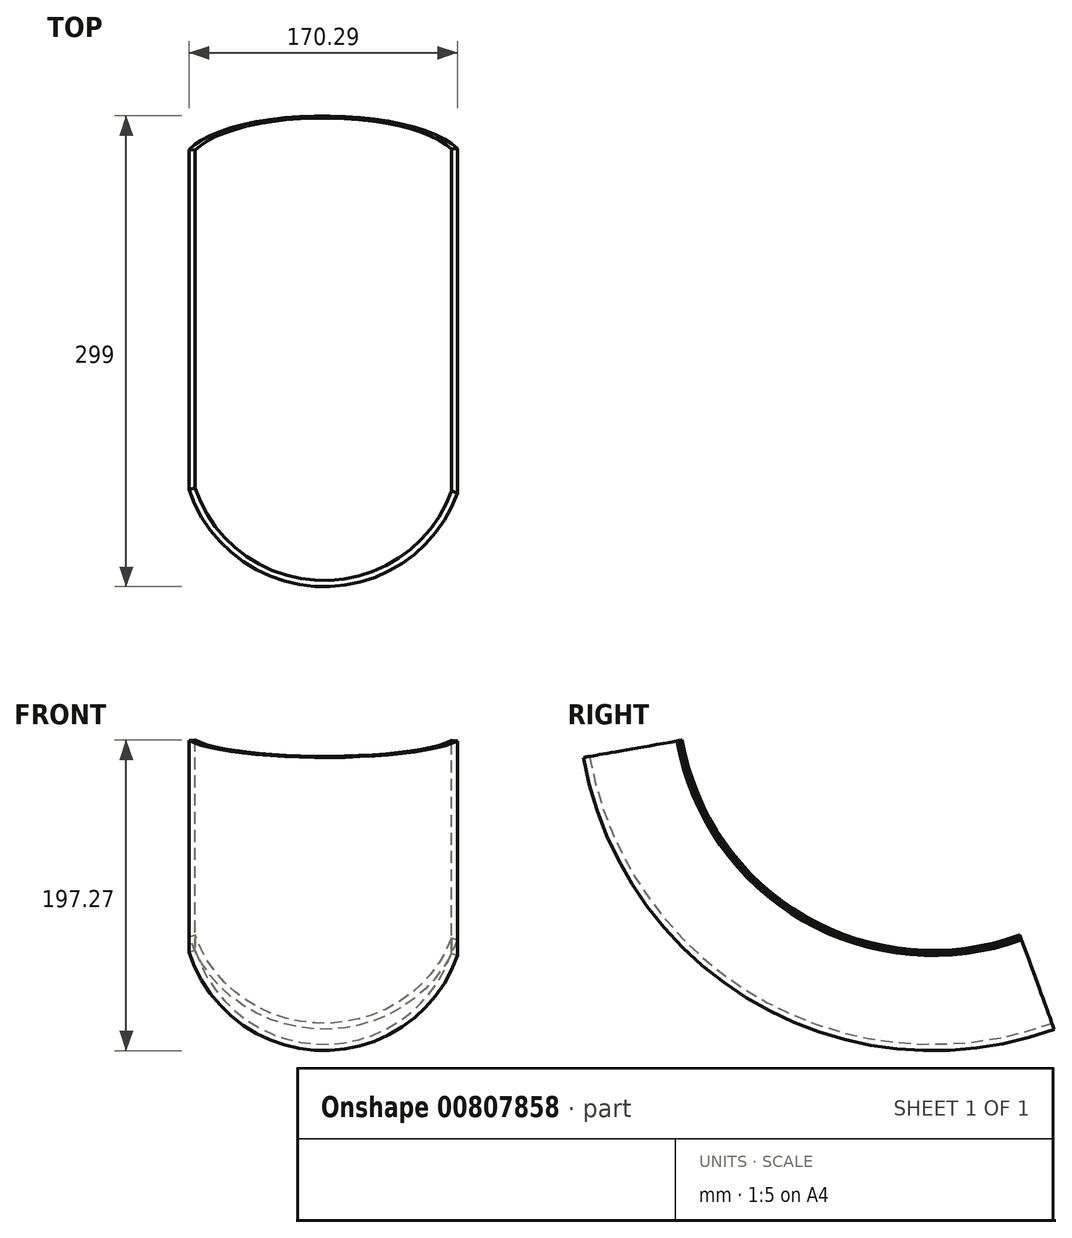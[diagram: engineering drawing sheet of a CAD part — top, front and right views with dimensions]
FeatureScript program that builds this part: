
annotation { "Feature Type Name" : "Feature", "Feature Type Description" : "" }
export const myFeature = defineFeature(function(context is Context, id is Id, definition is map)
    precondition{}
    {
        {
            var Q0;
            Q0=qCreatedBy(makeId("Front.planeOp"),FACE);
            var sketch = newSketch(context, id + "F0", { "sketchPlane" : qUnion([Q0])});
            skLineSegment(sketch, "E0", {"start": v(-109.57, 0) * mm, "end": v(134.88, 0) * mm});
            skPoint(sketch, "E1.middle", {"position": v(0, 0) * mm});
            skArc(sketch, "E2", {"start": v(75, 162.53) * mm, "mid": v(-0.66, 215) * mm, "end": v(-75, 160.68) * mm});
            skLineSegment(sketch, "E3", {"start": v(-75, 160.68) * mm, "end": v(-75, 0) * mm});
            skLineSegment(sketch, "E4", {"start": v(75, 162.53) * mm, "end": v(75, 0) * mm});
            skSolve(sketch);
        }
        {
            var Q0;
            Q0=qCreatedBy(makeId("Front.planeOp"),FACE);
            var sketch = newSketch(context, id + "F1", { "sketchPlane" : qUnion([Q0])});
            skArc(sketch, "E5.3", {"start": v(81.35, 163.62) * mm, "mid": v(-0.7, 221.34) * mm, "end": v(-81.35, 161.68) * mm});
            skArc(sketch, "E6.0", {"start": v(85.13, 164.92) * mm, "mid": v(-0.74, 225.34) * mm, "end": v(-85.16, 162.9) * mm});
            skLineSegment(sketch, "E7", {"start": v(-85.16, 162.9) * mm, "end": v(-81.35, 161.68) * mm});
            skLineSegment(sketch, "E8", {"start": v(81.35, 163.62) * mm, "end": v(85.13, 164.92) * mm});
            skSolve(sketch);
        }
        {
            var Q0;
            Q0 = qSketchRegion(id + "F1", true);
            var Q1;
            Q1=sQuery(id+"F0.wireOp",EDGE,"E0");
            revolve(context, id + "F2", {"surfaceOperationType" : NewSurfaceOperationType.NEW, "entities" : qUnion([Q0]), "axis" : qUnion([Q1]), "revolveType" : RevolveType.TWO_DIRECTIONS, "angle" : 200 * degree, "angleBack" : 100 * degree});
        }
    });
